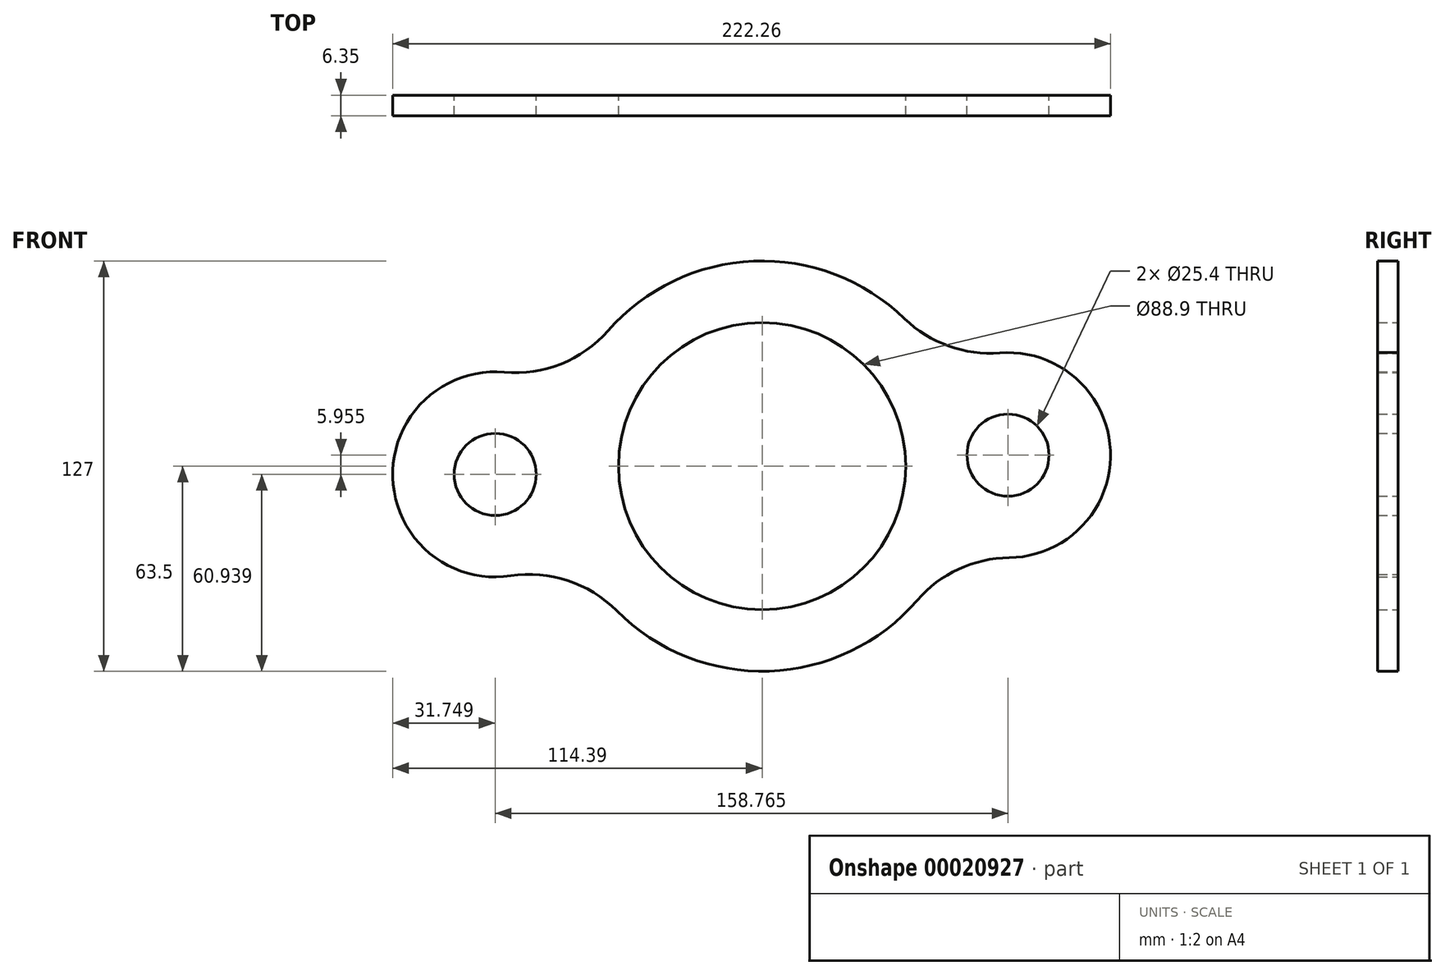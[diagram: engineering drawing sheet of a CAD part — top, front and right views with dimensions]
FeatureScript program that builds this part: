
annotation { "Feature Type Name" : "Feature", "Feature Type Description" : "" }
export const myFeature = defineFeature(function(context is Context, id is Id, definition is map)
    precondition{}
    {
        {
            var Q0;
            Q0=qCreatedBy(makeId("Front.planeOp"),FACE);
            var sketch = newSketch(context, id + "F0", { "sketchPlane" : qUnion([Q0])});
            skCircle(sketch, "E0", {"center": v(0, 0) * mm, "radius": 44.45 * mm});
            skCircle(sketch, "E1", {"center": v(-82.64, -2.56) * mm, "radius": 12.7 * mm});
            skCircle(sketch, "E2", {"center": v(76.12, 3.4) * mm, "radius": 12.7 * mm});
            skArc(sketch, "E3", {"start": v(-45.05, -44.75) * mm, "mid": v(2.2, -63.46) * mm, "end": v(48.03, -41.53) * mm});
            skArc(sketch, "E4", {"start": v(76.46, -28.35) * mm, "mid": v(107.84, 4.8) * mm, "end": v(73.63, 35.05) * mm});
            skArc(sketch, "E5", {"start": v(-79.8, 29.06) * mm, "mid": v(-114.38, -3.54) * mm, "end": v(-77.84, -33.95) * mm});
            skArc(sketch, "E6", {"start": v(-79.8, 29.06) * mm, "mid": v(-62.23, 31.63) * mm, "end": v(-47.73, 41.88) * mm});
            skArc(sketch, "E7", {"start": v(-45.05, -44.75) * mm, "mid": v(-60.15, -35.42) * mm, "end": v(-77.84, -33.95) * mm});
            skArc(sketch, "E8", {"start": v(44.15, 45.64) * mm, "mid": v(57.75, 37.17) * mm, "end": v(73.63, 35.05) * mm});
            skArc(sketch, "E9", {"start": v(76.46, -28.35) * mm, "mid": v(60.83, -31.89) * mm, "end": v(48.03, -41.53) * mm});
            skArc(sketch, "E10.trimOffspring", {"start": v(44.15, 45.64) * mm, "mid": v(-2.6, 63.45) * mm, "end": v(-47.73, 41.88) * mm});
            skSolve(sketch);
        }
        {
            var Q0;
            Q0 = qSketchRegion(id + "F0", true);
            extrude(context, id + "F1", {"entities" : qUnion([Q0]), "depth" : 6.35 * mm});
        }
    });
